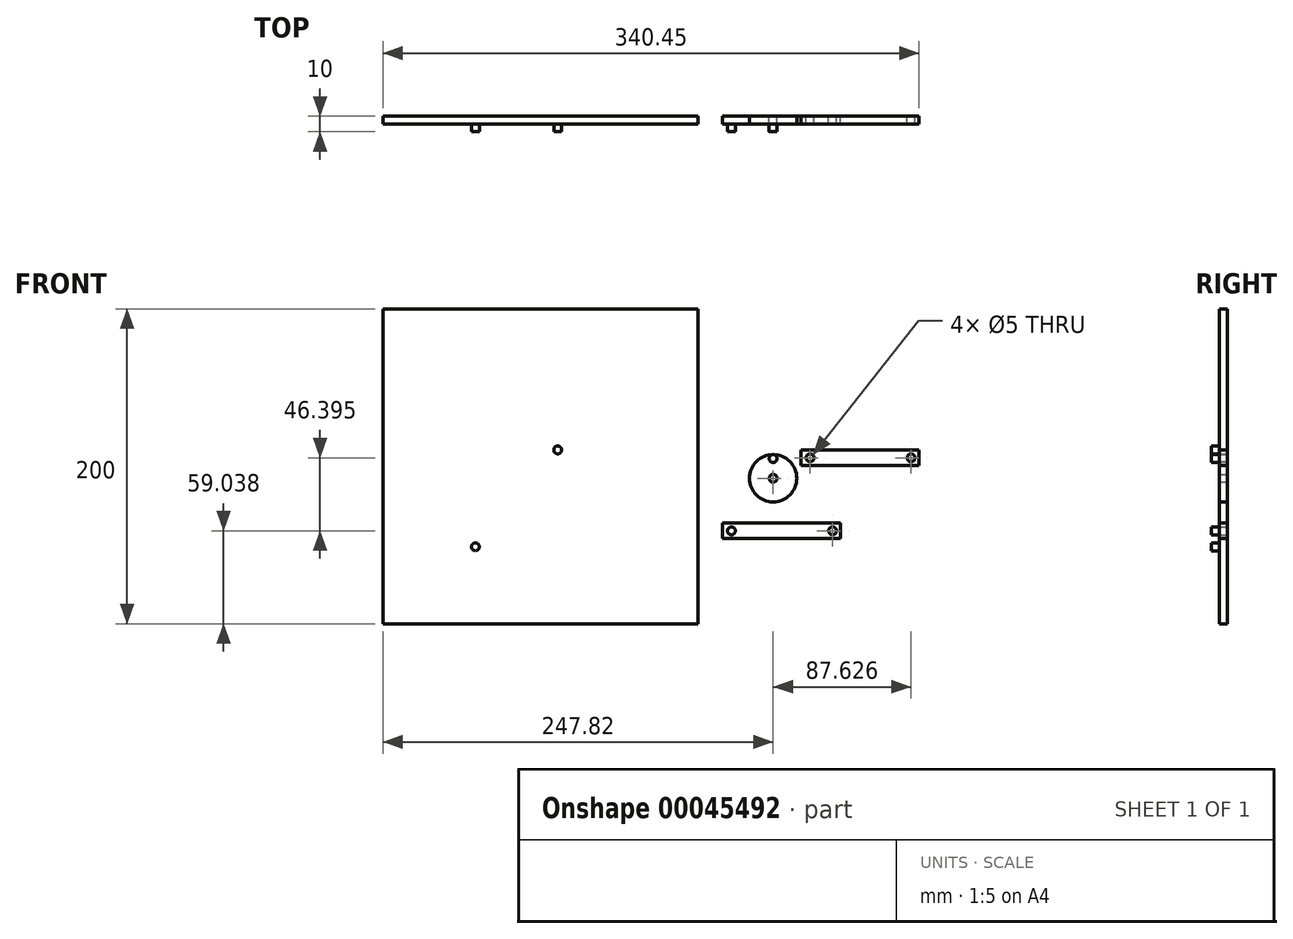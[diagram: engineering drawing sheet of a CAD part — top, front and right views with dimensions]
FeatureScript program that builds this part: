
annotation { "Feature Type Name" : "Feature", "Feature Type Description" : "" }
export const myFeature = defineFeature(function(context is Context, id is Id, definition is map)
    precondition{}
    {
        {
            var Q0;
            Q0=qCreatedBy(makeId("Front.planeOp"),FACE);
            var sketch = newSketch(context, id + "F0", { "sketchPlane" : qUnion([Q0])});
            skCircle(sketch, "E0", {"center": v(0, 0) * mm, "radius": 15 * mm});
            skCircle(sketch, "E1", {"center": v(0, 0) * mm, "radius": 2.5 * mm});
            skSolve(sketch);
        }
        {
            var Q0;
            Q0=makeQuery(id+"F0.imprint","IMPRINT",FACE,{"disambiguationData":[TD([[makeQuery(id+"F0.imprint","IMPRINT",EDGE,{"derivedFrom":sQuery(id+"F0.wireOp",EDGE,"E0")}),1.0]])]});
            extrude(context, id + "F1", {"entities" : qUnion([Q0]), "depth" : 5 * mm});
        }
        {
            var Q0;
            Q0=qCreatedBy(makeId("Front.planeOp"),FACE);
            var sketch = newSketch(context, id + "F2", { "sketchPlane" : qUnion([Q0])});
            skLineSegment(sketch, "E2.bottom", {"start": v(-47.82, 107.57) * mm, "end": v(-247.82, 107.57) * mm});
            skLineSegment(sketch, "E2.top", {"start": v(-47.82, -92.43) * mm, "end": v(-247.82, -92.43) * mm});
            skLineSegment(sketch, "E2.left", {"start": v(-47.82, 107.57) * mm, "end": v(-47.82, -92.43) * mm});
            skLineSegment(sketch, "E2.right", {"start": v(-247.82, 107.57) * mm, "end": v(-247.82, -92.43) * mm});
            skCircle(sketch, "E3", {"center": v(-189.08, -43.52) * mm, "radius": 2.5 * mm});
            skCircle(sketch, "E4", {"center": v(-136.8, 17.99) * mm, "radius": 2.5 * mm});
            skSolve(sketch);
        }
        {
            var Q0;
            Q0=makeQuery(id+"F2.imprint","IMPRINT",FACE,{"disambiguationData":[TD([[makeQuery(id+"F2.imprint","IMPRINT",EDGE,{"derivedFrom":sQuery(id+"F2.wireOp",EDGE,"E2.bottom")}),1.0]])]});
            extrude(context, id + "F3", {"entities" : qUnion([Q0]), "depth" : 5 * mm});
        }
        {
            var Q0;
            Q0=makeQuery(id+"F2.imprint","IMPRINT",FACE,{"disambiguationData":[TD([[makeQuery(id+"F2.imprint","IMPRINT",EDGE,{"derivedFrom":sQuery(id+"F2.wireOp",EDGE,"E3")}),1.0]])]});
            extrude(context, id + "F4", {"entities" : qUnion([Q0]), "operationType" : NewBodyOperationType.ADD, "depth" : 10 * mm});
        }
        {
            var Q0;
            Q0=makeQuery(id+"F1.opExtrude","CAP_FACE",FACE,{"disambiguationData":[OSD([sQuery(id+"F0.wireOp",EDGE,"E0"),sQuery(id+"F0.wireOp",EDGE,"E1")])],"isStart":false});
            var sketch = newSketch(context, id + "F5", { "sketchPlane" : qUnion([Q0])});
            skCircle(sketch, "E5", {"center": v(0, 12.5) * mm, "radius": 2.5 * mm});
            skSolve(sketch);
        }
        {
            var Q0;
            Q0=makeQuery(id+"F5.imprint","IMPRINT",FACE,{"disambiguationData":[TD([[makeQuery(id+"F5.imprint","IMPRINT",EDGE,{"derivedFrom":sQuery(id+"F5.wireOp",EDGE,"E5")}),1.0]])]});
            extrude(context, id + "F6", {"entities" : qUnion([Q0]), "operationType" : NewBodyOperationType.ADD, "depth" : 5 * mm});
        }
        {
            var Q0;
            Q0=qCreatedBy(makeId("Front.planeOp"),FACE);
            var sketch = newSketch(context, id + "F7", { "sketchPlane" : qUnion([Q0])});
            skLineSegment(sketch, "E6.bottom", {"start": v(17.63, 18) * mm, "end": v(92.63, 18) * mm});
            skLineSegment(sketch, "E6.top", {"start": v(17.63, 8) * mm, "end": v(92.63, 8) * mm});
            skLineSegment(sketch, "E6.left", {"start": v(17.63, 18) * mm, "end": v(17.63, 8) * mm});
            skLineSegment(sketch, "E6.right", {"start": v(92.63, 18) * mm, "end": v(92.63, 8) * mm});
            skCircle(sketch, "E7", {"center": v(23.44, 13) * mm, "radius": 2.5 * mm});
            skPoint(sketch, "E7.centerSnap0", {"position": v(17.63, 13) * mm});
            skCircle(sketch, "E8", {"center": v(87.63, 12.99) * mm, "radius": 2.5 * mm});
            skSolve(sketch);
        }
        {
            var Q0;
            Q0=makeQuery(id+"F7.imprint","IMPRINT",FACE,{"disambiguationData":[TD([[makeQuery(id+"F7.imprint","IMPRINT",EDGE,{"derivedFrom":sQuery(id+"F7.wireOp",EDGE,"E6.bottom")}),-1.0]])]});
            extrude(context, id + "F8", {"entities" : qUnion([Q0]), "depth" : 5 * mm});
        }
        {
            var Q0;
            Q0=qCreatedBy(makeId("Front.planeOp"),FACE);
            var sketch = newSketch(context, id + "F9", { "sketchPlane" : qUnion([Q0])});
            skLineSegment(sketch, "E9.bottom", {"start": v(-32.26, -28.4) * mm, "end": v(42.74, -28.4) * mm});
            skLineSegment(sketch, "E9.top", {"start": v(-32.26, -38.4) * mm, "end": v(42.74, -38.4) * mm});
            skLineSegment(sketch, "E9.left", {"start": v(-32.26, -28.4) * mm, "end": v(-32.26, -38.4) * mm});
            skLineSegment(sketch, "E9.right", {"start": v(42.74, -28.4) * mm, "end": v(42.74, -38.4) * mm});
            skCircle(sketch, "E10", {"center": v(-26.44, -33.4) * mm, "radius": 2.5 * mm});
            skPoint(sketch, "E10.centerSnap0", {"position": v(-32.26, -33.4) * mm});
            skCircle(sketch, "E11", {"center": v(37.74, -33.4) * mm, "radius": 2.5 * mm});
            skSolve(sketch);
        }
        {
            var Q0;
            Q0=makeQuery(id+"F9.imprint","IMPRINT",FACE,{"disambiguationData":[TD([[makeQuery(id+"F9.imprint","IMPRINT",EDGE,{"derivedFrom":sQuery(id+"F9.wireOp",EDGE,"E9.bottom")}),-1.0]])]});
            extrude(context, id + "F10", {"entities" : qUnion([Q0]), "depth" : 5 * mm});
        }
        {
            var Q0;
            Q0=makeQuery(id+"F9.imprint","IMPRINT",FACE,{"disambiguationData":[TD([[makeQuery(id+"F9.imprint","IMPRINT",EDGE,{"derivedFrom":sQuery(id+"F9.wireOp",EDGE,"E10")}),1.0]])]});
            extrude(context, id + "F11", {"entities" : qUnion([Q0]), "operationType" : NewBodyOperationType.ADD, "depth" : 10 * mm});
        }
        {
            var Q0;
            Q0=makeQuery(id+"F2.imprint","IMPRINT",FACE,{"disambiguationData":[TD([[makeQuery(id+"F2.imprint","IMPRINT",EDGE,{"derivedFrom":sQuery(id+"F2.wireOp",EDGE,"E4")}),1.0]])]});
            extrude(context, id + "F12", {"entities" : qUnion([Q0]), "operationType" : NewBodyOperationType.ADD, "depth" : 10 * mm});
        }
    });
